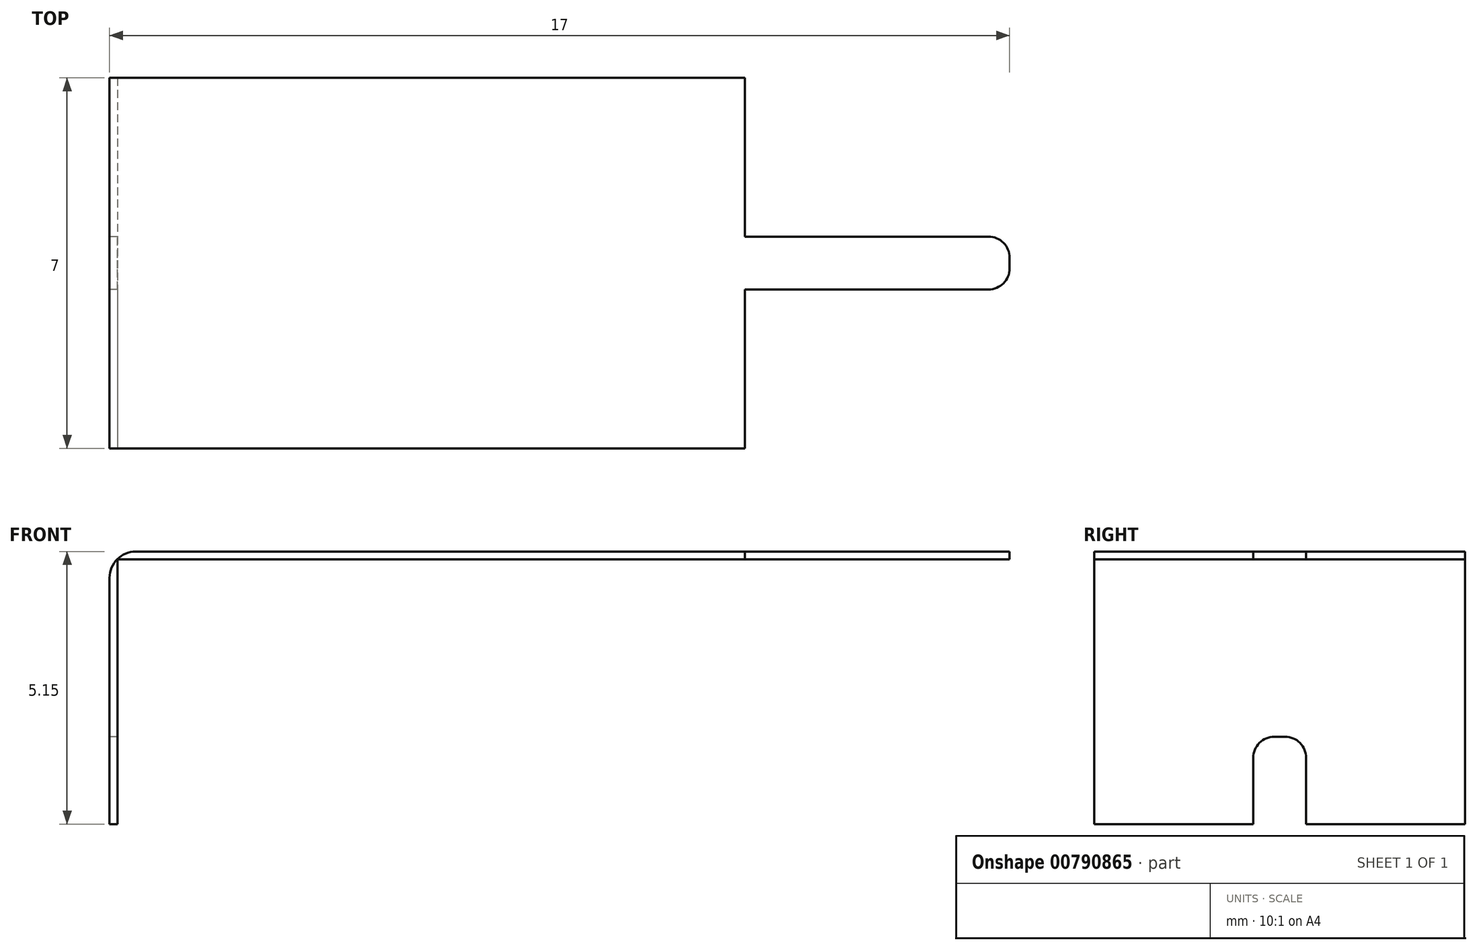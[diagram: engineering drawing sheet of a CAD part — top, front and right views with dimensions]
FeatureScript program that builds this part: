
annotation { "Feature Type Name" : "Feature", "Feature Type Description" : "" }
export const myFeature = defineFeature(function(context is Context, id is Id, definition is map)
    precondition{}
    {
        {
            var Q0;
            Q0=qCreatedBy(makeId("Top.planeOp"),FACE);
            var sketch = newSketch(context, id + "F0", { "sketchPlane" : qUnion([Q0])});
            skPoint(sketch, "E0.middle", {"position": v(0, 0) * mm});
            skLineSegment(sketch, "E1.bottom", {"start": v(-5.5, -0.5) * mm, "end": v(-10.1, -0.5) * mm});
            skLineSegment(sketch, "E1.top", {"start": v(-5.5, 0.5) * mm, "end": v(-10.1, 0.5) * mm});
            skLineSegment(sketch, "E1.left", {"start": v(-5.1, -0.1) * mm, "end": v(-5.1, 0.1) * mm});
            skLineSegment(sketch, "E1.right", {"start": v(-15.1, -0.1) * mm, "end": v(-15.1, 0.1) * mm});
            skPoint(sketch, "E1.middle", {"position": v(-10.1, 0) * mm});
            skPoint(sketch, "E2.visualSharp", {"position": v(-5.1, 0.5) * mm});
            skArc(sketch, "E2.filletArc", {"start": v(-5.1, 0.1) * mm, "mid": v(-5.22, 0.38) * mm, "end": v(-5.5, 0.5) * mm});
            skPoint(sketch, "E3.visualSharp", {"position": v(-5.1, -0.5) * mm});
            skArc(sketch, "E3.filletArc", {"start": v(-5.5, -0.5) * mm, "mid": v(-5.22, -0.38) * mm, "end": v(-5.1, -0.1) * mm});
            skPoint(sketch, "E4.visualSharp", {"position": v(-15.1, 0.5) * mm});
            skArc(sketch, "E4.filletArc", {"start": v(-14.7, 0.5) * mm, "mid": v(-14.98, 0.38) * mm, "end": v(-15.1, 0.1) * mm});
            skPoint(sketch, "E5.visualSharp", {"position": v(-15.1, -0.5) * mm});
            skArc(sketch, "E5.filletArc", {"start": v(-15.1, -0.1) * mm, "mid": v(-14.98, -0.38) * mm, "end": v(-14.7, -0.5) * mm});
            skLineSegment(sketch, "E6", {"start": v(0, 3.5) * mm, "end": v(-10.1, 3.5) * mm});
            skPoint(sketch, "E6.endSnap0", {"position": v(-10.1, 0.5) * mm});
            skLineSegment(sketch, "E7", {"start": v(-10.1, 3.5) * mm, "end": v(-10.1, 0.5) * mm});
            skLineSegment(sketch, "E8.MirrorCS", {"start": v(0, -3.5) * mm, "end": v(-10.1, -3.5) * mm});
            skLineSegment(sketch, "E9.MirrorCS", {"start": v(-10.1, -3.5) * mm, "end": v(-10.1, -0.5) * mm});
            skLineSegment(sketch, "E10.MirrorCS", {"start": v(0, 3.5) * mm, "end": v(10.1, 3.5) * mm});
            skLineSegment(sketch, "E11.MirrorCS", {"start": v(0, -3.5) * mm, "end": v(10.1, -3.5) * mm});
            skLineSegment(sketch, "E12.MirrorCS", {"start": v(5.1, -0.1) * mm, "end": v(5.1, 0.1) * mm});
            skArc(sketch, "E13.MirrorCS", {"start": v(5.1, 0.1) * mm, "mid": v(5.22, 0.38) * mm, "end": v(5.5, 0.5) * mm});
            skArc(sketch, "E14.MirrorCS", {"start": v(15.1, -0.1) * mm, "mid": v(14.98, -0.38) * mm, "end": v(14.7, -0.5) * mm});
            skLineSegment(sketch, "E15.MirrorCS", {"start": v(15.1, -0.1) * mm, "end": v(15.1, 0.1) * mm});
            skArc(sketch, "E16.MirrorCS", {"start": v(14.7, 0.5) * mm, "mid": v(14.98, 0.38) * mm, "end": v(15.1, 0.1) * mm});
            skArc(sketch, "E17.MirrorCS", {"start": v(5.5, -0.5) * mm, "mid": v(5.22, -0.38) * mm, "end": v(5.1, -0.1) * mm});
            skPoint(sketch, "E18.MirrorP", {"position": v(15.1, 0.5) * mm});
            skLineSegment(sketch, "E19.MirrorCS", {"start": v(5.5, 0.5) * mm, "end": v(14.7, 0.5) * mm});
            skLineSegment(sketch, "E20.MirrorCS", {"start": v(5.5, -0.5) * mm, "end": v(14.7, -0.5) * mm});
            skPoint(sketch, "E21.MirrorP", {"position": v(10.1, 0.5) * mm});
            skPoint(sketch, "E22.MirrorP", {"position": v(5.1, 0.5) * mm});
            skPoint(sketch, "E23.MirrorP", {"position": v(15.1, -0.5) * mm});
            skPoint(sketch, "E24.MirrorP", {"position": v(5.1, -0.5) * mm});
            skPoint(sketch, "E25.MirrorP", {"position": v(10.1, 0) * mm});
            skLineSegment(sketch, "E26.MirrorCS", {"start": v(10.1, 3.5) * mm, "end": v(10.1, 0.5) * mm});
            skLineSegment(sketch, "E27.MirrorCS", {"start": v(10.1, -3.5) * mm, "end": v(10.1, -0.5) * mm});
            skPoint(sketch, "E28.1.0.0", {"position": v(25.3, 0.5) * mm});
            skLineSegment(sketch, "E28.1.0.1", {"start": v(20.2, 3.5) * mm, "end": v(30.3, 3.5) * mm});
            skLineSegment(sketch, "E28.1.0.2", {"start": v(25.7, -0.5) * mm, "end": v(34.9, -0.5) * mm});
            skPoint(sketch, "E28.1.0.3", {"position": v(20.2, 0) * mm});
            skLineSegment(sketch, "E28.1.0.4", {"start": v(20.2, -3.5) * mm, "end": v(30.3, -3.5) * mm});
            skPoint(sketch, "E28.1.0.5", {"position": v(30.3, 0.5) * mm});
            skPoint(sketch, "E28.1.0.6", {"position": v(30.3, 0) * mm});
            skPoint(sketch, "E28.1.0.7", {"position": v(35.3, -0.5) * mm});
            skPoint(sketch, "E28.1.0.8", {"position": v(25.3, -0.5) * mm});
            skLineSegment(sketch, "E28.1.0.9", {"start": v(20.2, -3.5) * mm, "end": v(10.1, -3.5) * mm});
            skLineSegment(sketch, "E28.1.0.10", {"start": v(25.7, 0.5) * mm, "end": v(34.9, 0.5) * mm});
            skLineSegment(sketch, "E28.1.0.11", {"start": v(20.2, 3.5) * mm, "end": v(10.1, 3.5) * mm});
            skLineSegment(sketch, "E28.1.0.12", {"start": v(30.3, 3.5) * mm, "end": v(30.3, 0.5) * mm});
            skLineSegment(sketch, "E28.1.0.13", {"start": v(30.3, -3.5) * mm, "end": v(30.3, -0.5) * mm});
            skPoint(sketch, "E28.1.0.14", {"position": v(35.3, 0.5) * mm});
            skArc(sketch, "E28.1.0.15", {"start": v(34.9, 0.5) * mm, "mid": v(35.18, 0.38) * mm, "end": v(35.3, 0.1) * mm});
            skArc(sketch, "E28.1.0.16", {"start": v(25.7, -0.5) * mm, "mid": v(25.42, -0.38) * mm, "end": v(25.3, -0.1) * mm});
            skArc(sketch, "E28.1.0.17", {"start": v(35.3, -0.1) * mm, "mid": v(35.18, -0.38) * mm, "end": v(34.9, -0.5) * mm});
            skArc(sketch, "E28.1.0.18", {"start": v(25.3, 0.1) * mm, "mid": v(25.42, 0.38) * mm, "end": v(25.7, 0.5) * mm});
            skLineSegment(sketch, "E28.1.0.19", {"start": v(25.3, -0.1) * mm, "end": v(25.3, 0.1) * mm});
            skLineSegment(sketch, "E28.1.0.20", {"start": v(35.3, -0.1) * mm, "end": v(35.3, 0.1) * mm});
            skLineSegment(sketch, "E28.direction1", {"start": v(-10.1, -3.5) * mm, "end": v(10.1, -3.5) * mm, "construction": true});
            skLineSegment(sketch, "E29", {"start": v(0, 3.5) * mm, "end": v(0, -3.5) * mm});
            skLineSegment(sketch, "E30.bottom", {"start": v(70.7, -3.5) * mm, "end": v(73.7, -3.5) * mm});
            skLineSegment(sketch, "E30.top", {"start": v(70.7, 3.5) * mm, "end": v(73.7, 3.5) * mm});
            skLineSegment(sketch, "E30.left", {"start": v(70.7, -3.5) * mm, "end": v(70.7, 3.5) * mm});
            skLineSegment(sketch, "E30.right", {"start": v(73.7, -3.5) * mm, "end": v(73.7, 3.5) * mm});
            skSolve(sketch);
        }
        {
            var Q0;
            {var subQ8=sQuery(id+"F0.wireOp",EDGE,"E28.3.0.12");Q0=makeQuery(id+"F0.imprint","IMPRINT",FACE,{"disambiguationData":[TD([[makeQuery(id+"F0.imprint","IMPRINT",EDGE,{"derivedFrom":subQ8}),1.0]])]});}
            var Q1;
            {var subQ3=sQuery(id+"F0.wireOp",EDGE,"E14.MirrorCS");Q1=makeQuery(id+"F0.imprint","IMPRINT",FACE,{"disambiguationData":[TD([[makeQuery(id+"F0.imprint","IMPRINT",EDGE,{"derivedFrom":subQ3}),1.0]])]});}
            var Q2;
            {var subQ8=sQuery(id+"F0.wireOp",EDGE,"E28.1.0.12");Q2=makeQuery(id+"F0.imprint","IMPRINT",FACE,{"disambiguationData":[TD([[makeQuery(id+"F0.imprint","IMPRINT",EDGE,{"derivedFrom":subQ8}),1.0]])]});}
            var Q3;
            {var subQ8=sQuery(id+"F0.wireOp",EDGE,"E28.2.0.12");Q3=makeQuery(id+"F0.imprint","IMPRINT",FACE,{"disambiguationData":[TD([[makeQuery(id+"F0.imprint","IMPRINT",EDGE,{"derivedFrom":subQ8}),1.0]])]});}
            var Q4;
            Q4=makeQuery(id+"F0.imprint","IMPRINT",FACE,{"disambiguationData":[TD([[makeQuery(id+"F0.imprint","IMPRINT",EDGE,{"derivedFrom":sQuery(id+"F0.wireOp",EDGE,"E10.MirrorCS")}),-1.0]])]});
            extrude(context, id + "F1", {"entities" : qUnion([Q0, Q1, Q2, Q3, Q4]), "depth" : 0.15 * mm, "offsetDistance" : 25 * mm});
        }
        {
            var Q0;
            Q0=makeQuery(id+"F1.opExtrude","SWEPT_FACE",FACE,{"disambiguationData":[OSD([sQuery(id+"F0.wireOp",EDGE,"E29")])]});
            extrude(context, id + "F2", {"entities" : qUnion([Q0]), "operationType" : NewBodyOperationType.ADD, "depth" : 1.9 * mm, "offsetDistance" : 25 * mm});
        }
        {
            var Q0;
            {var subQ0=sQuery(id+"F0.wireOp",EDGE,"E29");Q0=makeQuery(id+"F2.boolean.opBoolean","MERGE",FACE,{"derivedFrom":[makeQuery(id+"F1.opExtrude","CAP_FACE",FACE,{"disambiguationData":[OSD([sQuery(id+"F0.wireOp",EDGE,"E10.MirrorCS"),sQuery(id+"F0.wireOp",EDGE,"E11.MirrorCS"),sQuery(id+"F0.wireOp",EDGE,"E12.MirrorCS"),sQuery(id+"F0.wireOp",EDGE,"E13.MirrorCS"),sQuery(id+"F0.wireOp",EDGE,"E14.MirrorCS"),sQuery(id+"F0.wireOp",EDGE,"E15.MirrorCS"),sQuery(id+"F0.wireOp",EDGE,"E16.MirrorCS"),sQuery(id+"F0.wireOp",EDGE,"E17.MirrorCS"),sQuery(id+"F0.wireOp",EDGE,"E19.MirrorCS"),sQuery(id+"F0.wireOp",EDGE,"E20.MirrorCS"),sQuery(id+"F0.wireOp",EDGE,"E28.1.0.1"),sQuery(id+"F0.wireOp",EDGE,"E28.1.0.2"),sQuery(id+"F0.wireOp",EDGE,"E28.1.0.4"),sQuery(id+"F0.wireOp",EDGE,"E28.1.0.9"),sQuery(id+"F0.wireOp",EDGE,"E28.1.0.10"),sQuery(id+"F0.wireOp",EDGE,"E28.1.0.11"),sQuery(id+"F0.wireOp",EDGE,"E28.1.0.15"),sQuery(id+"F0.wireOp",EDGE,"E28.1.0.16"),sQuery(id+"F0.wireOp",EDGE,"E28.1.0.17"),sQuery(id+"F0.wireOp",EDGE,"E28.1.0.18"),sQuery(id+"F0.wireOp",EDGE,"E28.1.0.19"),sQuery(id+"F0.wireOp",EDGE,"E28.1.0.20"),sQuery(id+"F0.wireOp",EDGE,"E28.2.0.1"),sQuery(id+"F0.wireOp",EDGE,"E28.2.0.2"),sQuery(id+"F0.wireOp",EDGE,"E28.2.0.4"),sQuery(id+"F0.wireOp",EDGE,"E28.2.0.9"),sQuery(id+"F0.wireOp",EDGE,"E28.2.0.10"),sQuery(id+"F0.wireOp",EDGE,"E28.2.0.11"),sQuery(id+"F0.wireOp",EDGE,"E28.2.0.15"),sQuery(id+"F0.wireOp",EDGE,"E28.2.0.16"),sQuery(id+"F0.wireOp",EDGE,"E28.2.0.17"),sQuery(id+"F0.wireOp",EDGE,"E28.2.0.18"),sQuery(id+"F0.wireOp",EDGE,"E28.2.0.19"),sQuery(id+"F0.wireOp",EDGE,"E28.2.0.20"),sQuery(id+"F0.wireOp",EDGE,"E28.3.0.1"),sQuery(id+"F0.wireOp",EDGE,"E28.3.0.2"),sQuery(id+"F0.wireOp",EDGE,"E28.3.0.4"),sQuery(id+"F0.wireOp",EDGE,"E28.3.0.9"),sQuery(id+"F0.wireOp",EDGE,"E28.3.0.10"),sQuery(id+"F0.wireOp",EDGE,"E28.3.0.11"),sQuery(id+"F0.wireOp",EDGE,"E28.3.0.12"),sQuery(id+"F0.wireOp",EDGE,"E28.3.0.13"),sQuery(id+"F0.wireOp",EDGE,"E28.3.0.16"),sQuery(id+"F0.wireOp",EDGE,"E28.3.0.18"),sQuery(id+"F0.wireOp",EDGE,"E28.3.0.19"),subQ0])],"isStart":true}),makeQuery(id+"F2.opExtrude","SWEPT_FACE",FACE,{"disambiguationData":[OSD([subQ0]),TDD([makeQuery(id+"F1.opExtrude","CAP_EDGE",EDGE,{"disambiguationData":[OSD([subQ0])],"isStart":true})])]})]});}
            var sketch = newSketch(context, id + "F3", { "sketchPlane" : qUnion([Q0])});
            skLineSegment(sketch, "E31.bottom", {"start": v(-1.9, -3.5) * mm, "end": v(-1.75, -3.5) * mm});
            skLineSegment(sketch, "E31.top", {"start": v(-1.9, 3.5) * mm, "end": v(-1.75, 3.5) * mm});
            skLineSegment(sketch, "E31.left", {"start": v(-1.9, -3.5) * mm, "end": v(-1.9, 3.5) * mm});
            skLineSegment(sketch, "E31.right", {"start": v(-1.75, -3.5) * mm, "end": v(-1.75, 3.5) * mm});
            skSolve(sketch);
        }
        {
            var Q0;
            Q0=qSketchRegion(id+"F3",true);
            extrude(context, id + "F4", {"entities" : qUnion([Q0]), "operationType" : NewBodyOperationType.ADD, "depth" : 5 * mm, "offsetDistance" : 25 * mm});
        }
        {
            var Q0;
            Q0=makeQuery(id+"F4.boolean.opBoolean","MERGE",FACE,{"derivedFrom":[makeQuery(id+"F2.opExtrude","CAP_FACE",FACE,{"disambiguationData":[OSD([sQuery(id+"F0.wireOp",EDGE,"E29")])],"isStart":false}),makeQuery(id+"F4.opExtrude","SWEPT_FACE",FACE,{"disambiguationData":[OSD([sQuery(id+"F3.wireOp",EDGE,"E31.left")])]})]});
            var sketch = newSketch(context, id + "F5", { "sketchPlane" : qUnion([Q0])});
            skLineSegment(sketch, "E32.bottom", {"start": v(0.1, -3.35) * mm, "end": v(-0.1, -3.35) * mm});
            skLineSegment(sketch, "E32.top", {"start": v(0.5, -13.35) * mm, "end": v(-0.5, -13.35) * mm});
            skLineSegment(sketch, "E32.left", {"start": v(0.5, -3.75) * mm, "end": v(0.5, -13.35) * mm});
            skLineSegment(sketch, "E32.right", {"start": v(-0.5, -3.75) * mm, "end": v(-0.5, -13.35) * mm});
            skPoint(sketch, "E32.middle", {"position": v(0, -8.35) * mm});
            skPoint(sketch, "E32.middle.positionSnap0", {"position": v(0, -5) * mm});
            skPoint(sketch, "E32.centerSnap0", {"position": v(0, -5) * mm});
            skPoint(sketch, "E33.visualSharp", {"position": v(-0.5, -3.35) * mm});
            skArc(sketch, "E33.filletArc", {"start": v(-0.1, -3.35) * mm, "mid": v(-0.38, -3.47) * mm, "end": v(-0.5, -3.75) * mm});
            skPoint(sketch, "E34.visualSharp", {"position": v(0.5, -3.35) * mm});
            skArc(sketch, "E34.filletArc", {"start": v(0.5, -3.75) * mm, "mid": v(0.38, -3.47) * mm, "end": v(0.1, -3.35) * mm});
            skSolve(sketch);
        }
        {
            var Q0;
            Q0=makeQuery(id+"F5.imprint","IMPRINT",FACE,{"disambiguationData":[TD([[makeQuery(id+"F5.imprint","IMPRINT",EDGE,{"derivedFrom":sQuery(id+"F5.wireOp",EDGE,"E32.bottom")}),1.0]])]});
            extrude(context, id + "F6", {"entities" : qUnion([Q0]), "operationType" : NewBodyOperationType.REMOVE, "oppositeDirection" : true, "depth" : 25 * mm, "offsetDistance" : 25 * mm});
        }
        {
            var Q0;
            {var subQ0=sQuery(id+"F0.wireOp",EDGE,"E29");Q0=makeQuery(id+"F2.opExtrude","CAP_EDGE",EDGE,{"disambiguationData":[OSD([subQ0]),TDD([makeQuery(id+"F1.opExtrude","CAP_EDGE",EDGE,{"disambiguationData":[OSD([subQ0])],"isStart":false})])],"isStart":false});}
            var Q1;
            Q1=makeQuery(id+"F4.opExtrude","CAP_EDGE",EDGE,{"disambiguationData":[OSD([sQuery(id+"F3.wireOp",EDGE,"E31.right")])],"isStart":true});
            fillet(context, id + "F7", {"entities" : qUnion([Q0, Q1]), "radius" : 0.5 * mm, "tangentPropagation" : true, "allowEdgeOverflow" : false});
        }
    });
